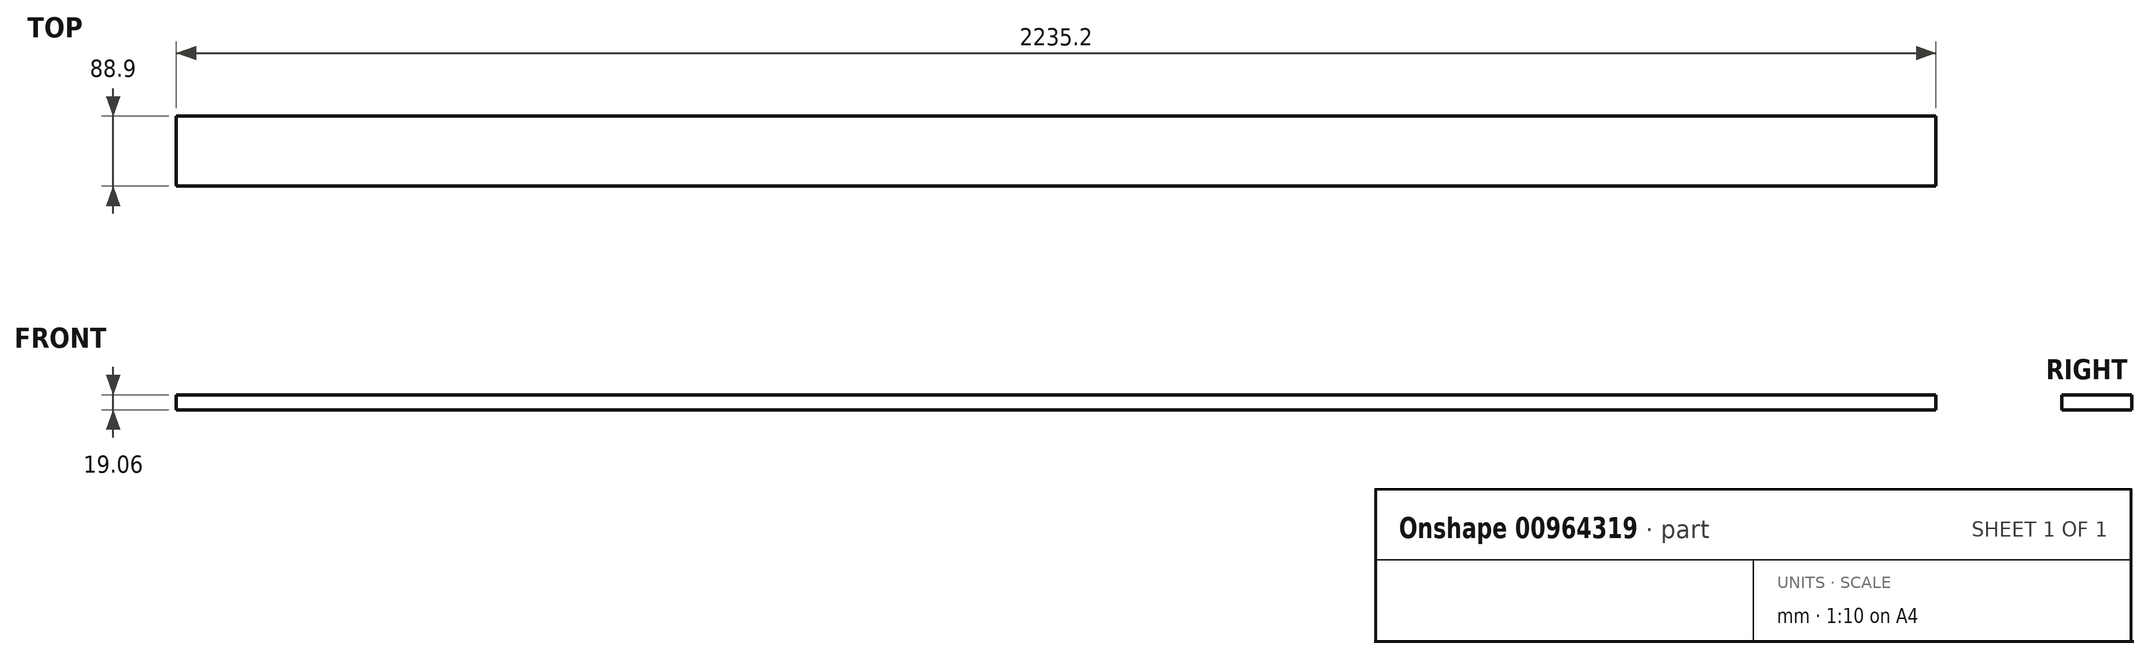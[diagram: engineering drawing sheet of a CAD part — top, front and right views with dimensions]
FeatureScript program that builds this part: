
annotation { "Feature Type Name" : "Feature", "Feature Type Description" : "" }
export const myFeature = defineFeature(function(context is Context, id is Id, definition is map)
    precondition{}
    {
        {
            var Q0;
            Q0=qCreatedBy(makeId("Right.planeOp"),FACE);
            var sketch = newSketch(context, id + "F0", { "sketchPlane" : qUnion([Q0])});
            skLineSegment(sketch, "E0.bottom", {"start": v(-44.45, 9.53) * mm, "end": v(44.45, 9.53) * mm});
            skLineSegment(sketch, "E0.top", {"start": v(-44.45, -9.53) * mm, "end": v(44.45, -9.53) * mm});
            skLineSegment(sketch, "E0.left", {"start": v(-44.45, 9.53) * mm, "end": v(-44.45, -9.53) * mm});
            skLineSegment(sketch, "E0.right", {"start": v(44.45, 9.53) * mm, "end": v(44.45, -9.53) * mm});
            skPoint(sketch, "E0.middle", {"position": v(0, 0) * mm});
            skSolve(sketch);
        }
        {
            var Q0;
            Q0 = qSketchRegion(id + "F0", true);
            extrude(context, id + "F1", {"entities" : qUnion([Q0]), "endBound" : BoundingType.SYMMETRIC, "depth" : 2235.2 * mm, "offsetDistance" : 25.4 * mm});
        }
    });
